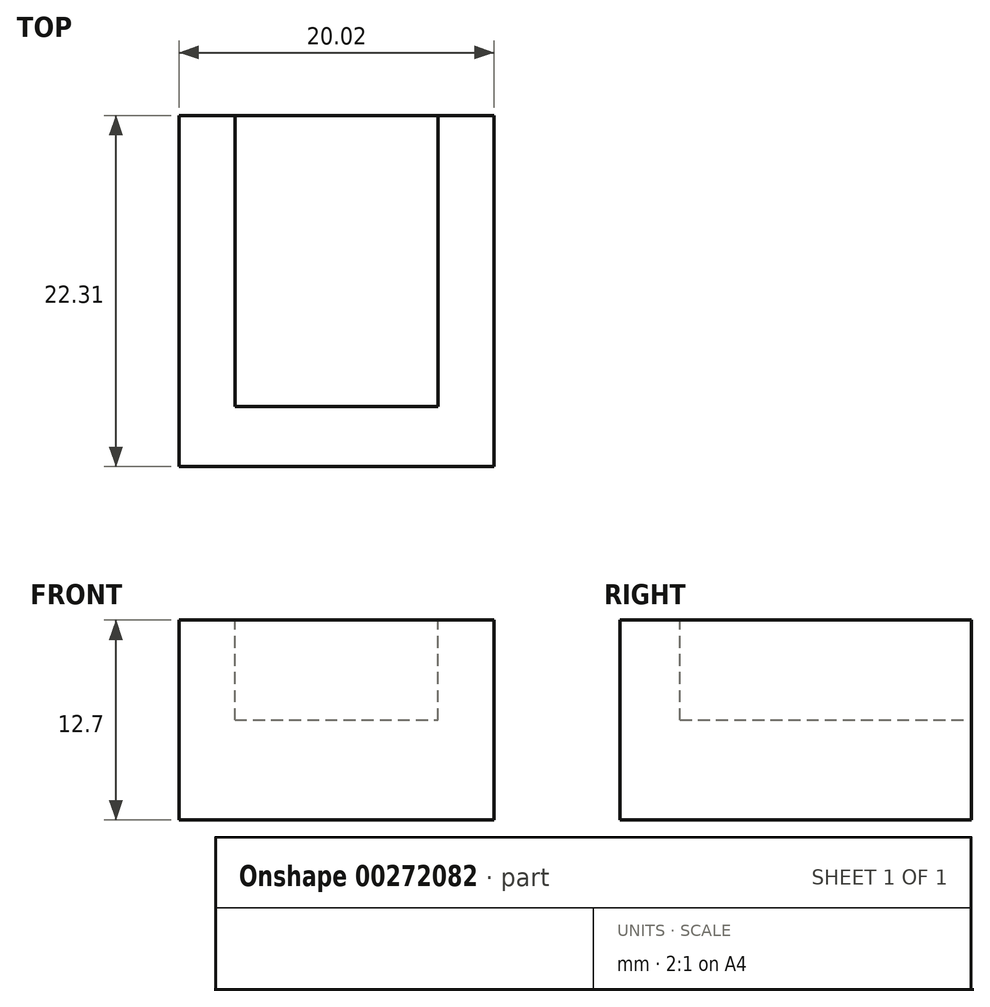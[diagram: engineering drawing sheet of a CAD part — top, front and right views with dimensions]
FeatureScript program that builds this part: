
annotation { "Feature Type Name" : "Feature", "Feature Type Description" : "" }
export const myFeature = defineFeature(function(context is Context, id is Id, definition is map)
    precondition{}
    {
        {
            var Q0;
            Q0=qCreatedBy(makeId("Top.planeOp"),FACE);
            var sketch = newSketch(context, id + "F0", { "sketchPlane" : qUnion([Q0])});
            skLineSegment(sketch, "E0.bottom", {"start": v(-9.84, -6.88) * mm, "end": v(2.56, -6.88) * mm});
            skLineSegment(sketch, "E0.top", {"start": v(-9.84, -25.38) * mm, "end": v(2.56, -25.38) * mm});
            skLineSegment(sketch, "E0.left", {"start": v(-9.84, -6.88) * mm, "end": v(-9.84, -25.38) * mm});
            skLineSegment(sketch, "E0.right", {"start": v(2.56, -6.88) * mm, "end": v(2.56, -25.38) * mm});
            skSolve(sketch);
        }
        {
            var Q0;
            Q0 = qSketchRegion(id + "F0", true);
            extrude(context, id + "F1", {"entities" : qUnion([Q0]), "depth" : 6.35 * mm});
        }
        {
            var Q0;
            Q0=makeQuery(id+"F1.opExtrude","SWEPT_FACE",FACE,{"disambiguationData":[OSD([sQuery(id+"F0.wireOp",EDGE,"E0.top")])]});
            var sketch = newSketch(context, id + "F2", { "sketchPlane" : qUnion([Q0])});
            skLineSegment(sketch, "E1.bottom", {"start": v(-9.84, 0) * mm, "end": v(2.56, 0) * mm});
            skLineSegment(sketch, "E1.top", {"start": v(-9.84, 12.7) * mm, "end": v(2.56, 12.7) * mm});
            skLineSegment(sketch, "E1.left", {"start": v(-9.84, 0) * mm, "end": v(-9.84, 12.7) * mm});
            skLineSegment(sketch, "E1.right", {"start": v(2.56, 0) * mm, "end": v(2.56, 12.7) * mm});
            skSolve(sketch);
        }
        {
            var Q0;
            Q0 = qSketchRegion(id + "F2", true);
            extrude(context, id + "F3", {"entities" : qUnion([Q0]), "operationType" : NewBodyOperationType.ADD, "depth" : 3.8 * mm});
        }
        {
            var Q0;
            Q0=makeQuery(id+"F3.boolean.opBoolean","MERGE",FACE,{"derivedFrom":[makeQuery(id+"F1.opExtrude","SWEPT_FACE",FACE,{"disambiguationData":[OSD([sQuery(id+"F0.wireOp",EDGE,"E0.right")])]}),makeQuery(id+"F3.opExtrude","SWEPT_FACE",FACE,{"disambiguationData":[OSD([sQuery(id+"F2.wireOp",EDGE,"E1.right")])]})]});
            var sketch = newSketch(context, id + "F4", { "sketchPlane" : qUnion([Q0])});
            skLineSegment(sketch, "E2.bottom", {"start": v(-29.2, 0) * mm, "end": v(-6.88, 0) * mm});
            skLineSegment(sketch, "E2.top", {"start": v(-29.2, 12.7) * mm, "end": v(-6.88, 12.7) * mm});
            skLineSegment(sketch, "E2.left", {"start": v(-29.2, 0) * mm, "end": v(-29.2, 12.7) * mm});
            skLineSegment(sketch, "E2.right", {"start": v(-6.88, 0) * mm, "end": v(-6.88, 12.7) * mm});
            skSolve(sketch);
        }
        {
            var Q0;
            Q0 = qSketchRegion(id + "F4", true);
            extrude(context, id + "F5", {"entities" : qUnion([Q0]), "operationType" : NewBodyOperationType.ADD, "depth" : 3.8 * mm});
        }
        {
            var Q0;
            Q0=makeQuery(id+"F3.boolean.opBoolean","MERGE",FACE,{"derivedFrom":[makeQuery(id+"F1.opExtrude","SWEPT_FACE",FACE,{"disambiguationData":[OSD([sQuery(id+"F0.wireOp",EDGE,"E0.left")])]}),makeQuery(id+"F3.opExtrude","SWEPT_FACE",FACE,{"disambiguationData":[OSD([sQuery(id+"F2.wireOp",EDGE,"E1.left")])]})]});
            var sketch = newSketch(context, id + "F6", { "sketchPlane" : qUnion([Q0])});
            skLineSegment(sketch, "E3.bottom", {"start": v(6.88, 0) * mm, "end": v(29.2, 0) * mm});
            skLineSegment(sketch, "E3.top", {"start": v(6.88, 12.7) * mm, "end": v(29.2, 12.7) * mm});
            skLineSegment(sketch, "E3.left", {"start": v(6.88, 0) * mm, "end": v(6.88, 12.7) * mm});
            skLineSegment(sketch, "E3.right", {"start": v(29.2, 0) * mm, "end": v(29.2, 12.7) * mm});
            skSolve(sketch);
        }
        {
            var Q0;
            Q0 = qSketchRegion(id + "F6", true);
            extrude(context, id + "F7", {"entities" : qUnion([Q0]), "operationType" : NewBodyOperationType.ADD, "depth" : 3.8 * mm});
        }
        {
            var Q0;
            Q0=makeQuery(id+"F7.boolean.opBoolean","MERGE",FACE,{"derivedFrom":[makeQuery(id+"F5.boolean.opBoolean","MERGE",FACE,{"derivedFrom":[makeQuery(id+"F3.opExtrude","SWEPT_FACE",FACE,{"disambiguationData":[OSD([sQuery(id+"F2.wireOp",EDGE,"E1.top")])]}),makeQuery(id+"F5.opExtrude","SWEPT_FACE",FACE,{"disambiguationData":[OSD([sQuery(id+"F4.wireOp",EDGE,"E2.top")])]})]}),makeQuery(id+"F7.opExtrude","SWEPT_FACE",FACE,{"disambiguationData":[OSD([sQuery(id+"F6.wireOp",EDGE,"E3.top")])]})]});
            var sketch = newSketch(context, id + "F8", { "sketchPlane" : qUnion([Q0])});
            skLineSegment(sketch, "E4.bottom", {"start": v(2.82, -6.88) * mm, "end": v(-10.1, -6.88) * mm});
            skLineSegment(sketch, "E4.top", {"start": v(2.82, -25.38) * mm, "end": v(-10.1, -25.38) * mm});
            skLineSegment(sketch, "E4.left", {"start": v(2.82, -6.88) * mm, "end": v(2.82, -25.38) * mm});
            skLineSegment(sketch, "E4.right", {"start": v(-10.1, -6.88) * mm, "end": v(-10.1, -25.38) * mm});
            skSolve(sketch);
        }
        {
            var Q0;
            Q0 = qSketchRegion(id + "F8", true);
            var Q1;
            Q1=makeQuery(id+"F1.opExtrude","CAP_FACE",FACE,{"disambiguationData":[OSD([sQuery(id+"F0.wireOp",EDGE,"E0.bottom"),sQuery(id+"F0.wireOp",EDGE,"E0.top"),sQuery(id+"F0.wireOp",EDGE,"E0.left"),sQuery(id+"F0.wireOp",EDGE,"E0.right")])],"isStart":false});
            extrude(context, id + "F9", {"entities" : qUnion([Q0]), "operationType" : NewBodyOperationType.REMOVE, "endBound" : BoundingType.UP_TO_SURFACE, "oppositeDirection" : true, "endBoundEntityFace" : qUnion([Q1]), "depth" : 6.35 * mm});
        }
    });
